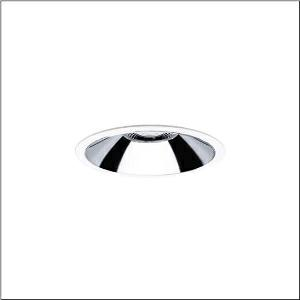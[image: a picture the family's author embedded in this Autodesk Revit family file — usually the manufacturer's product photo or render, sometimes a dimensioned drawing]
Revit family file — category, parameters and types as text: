
# Revit family: lunis_21_xl_51db15df42
name_source: partatom
category: Lighting Fixtures
units: mm (PartAtom-declared; Revit-internal decimal feet)

## family parameters
Cut with Voids When Loaded = No
Host = Face
Light Source = No
Part Type = Normal
Room Calculation Point = No
Round Connector Dimension = Use Diameter
Shared = No

## types (1)
- Lunis 21 XL (1 x LED, 2280 lm, 17.7 W, 4000K)
    Apparent Load = 18 VA
    CIE Flux Codes = 89 99 100 100 100
    Color Rendering = 80
    Color Temperature = 4000K
    Default Elevation = 1800 mm
    Description = Lunis 21,  XL, downlight, of PC, light emission: direct distribution, LED rated luminous flux: 2.280lm, light colour: 840, control gear: ECG DALI, with terminal, 5-pole, mains connection: 220..240V, AC, housing, round, of diecast aluminium, traffic white (RAL 9016), diameter: 213mm, protection rating (complete): IP20, protection rating (on room side): IP54, insulation class (complete): insulation class II (safety insulation), certification: CE, impact resistance: IK02, packaging unit: 1 piece
    Height = 0 mm  [stored 0 ft]
    Lamp = 1 x LED
    Lamp Light Flux = 2280 lm
    Lamp Power = 17.7 W
    Lamp count = 1
    Length = 213 mm
    Luminous efficacy = 129 lm/W
    Manufacturer = Siteco
    ModVariant = No
    Model = 51DB15DF42
    Mounting Place = Ceiling
    Mounting Type = Recessed
    Number of Poles = 1
    OnlyDefault = Yes
    Power Factor = 1
    Product Name = Lunis 21 XL
    Product group = downlight
    ProductGroupID = 400
    Protection Class = Protection class II
    Protection Degree = IP 20
    RLX_Detail_Level = 1
    RLX_Emergency_Light_Flux = 0 lm
    RLX_Emergency_Type = 0
    RLX_Emergency_Type_DB = No
    RlxData = <blob elided: 26925 chars, md5=1048c6de>
    Socket = socket
    Standby Power = 0 W
    System Light Flux = 2280 lm
    System Power = 18 W
    Type Comments = Product without accessories
    Type Image = l_1287385.jpg
    URL = http://relux.com
    VarID = ---
    Voltage = 0 V
    Weight = 0.00 kg
    Width = 0 mm  [stored 0 ft]

note: [stored X ft] marks values corroborated as IEEE doubles in the binary element streams (Revit-internal decimal feet)

## geometry (parser evidence)
native form markers: Blend x4, Sweep x11
no freeform markers — native parametric forms only
